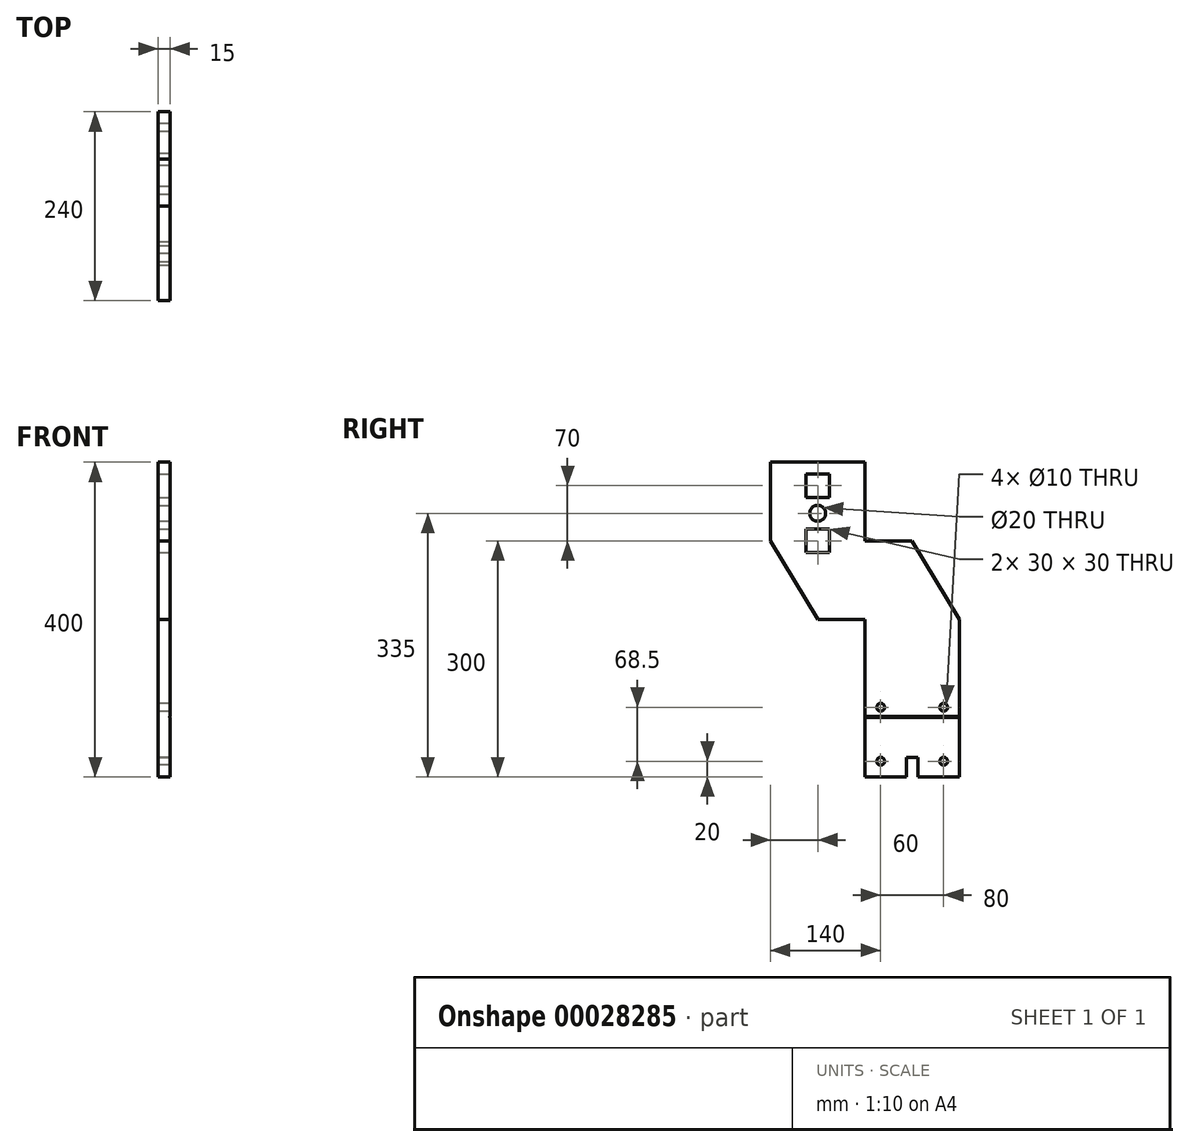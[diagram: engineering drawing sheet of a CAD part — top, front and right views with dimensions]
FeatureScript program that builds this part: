
annotation { "Feature Type Name" : "Feature", "Feature Type Description" : "" }
export const myFeature = defineFeature(function(context is Context, id is Id, definition is map)
    precondition{}
    {
        {
            var Q0;
            Q0=qCreatedBy(makeId("Right.planeOp"),FACE);
            var sketch = newSketch(context, id + "F0", { "sketchPlane" : qUnion([Q0])});
            skLineSegment(sketch, "E0.bottom", {"start": v(0, 0) * mm, "end": v(120, 0) * mm});
            skLineSegment(sketch, "E0.left", {"start": v(0, 0) * mm, "end": v(0, 200) * mm});
            skLineSegment(sketch, "E0.right", {"start": v(120, 0) * mm, "end": v(120, 200) * mm});
            skLineSegment(sketch, "E1", {"start": v(0, 200) * mm, "end": v(-60, 200) * mm});
            skLineSegment(sketch, "E2", {"start": v(0, 400) * mm, "end": v(-120, 400) * mm});
            skLineSegment(sketch, "E3", {"start": v(120, 200) * mm, "end": v(60, 300) * mm});
            skPoint(sketch, "E0.top.end.orphan", {"position": v(120, 400) * mm});
            skLineSegment(sketch, "E4", {"start": v(-60, 200) * mm, "end": v(-120, 300) * mm});
            skLineSegment(sketch, "E5", {"start": v(-120, 300) * mm, "end": v(-120, 400) * mm});
            skLineSegment(sketch, "E6", {"start": v(0, 400) * mm, "end": v(0, 300) * mm});
            skLineSegment(sketch, "E7", {"start": v(0, 300) * mm, "end": v(60, 300) * mm});
            skPoint(sketch, "E8.orphan", {"position": v(-180, 400) * mm});
            skSolve(sketch);
        }
        {
            var Q0;
            Q0=makeQuery(id+"F0.imprint","IMPRINT",FACE,{"disambiguationData":[TD([[makeQuery(id+"F0.imprint","IMPRINT",EDGE,{"derivedFrom":sQuery(id+"F0.wireOp",EDGE,"E0.bottom")}),1.0]])]});
            var sketch = newSketch(context, id + "F1", { "sketchPlane" : qUnion([Q0])});
            skCircle(sketch, "E9", {"center": v(20, 20) * mm, "radius": 5 * mm});
            skCircle(sketch, "E10.MirrorC", {"center": v(100, 20) * mm, "radius": 5 * mm});
            skCircle(sketch, "E11.MirrorC", {"center": v(100, 88.5) * mm, "radius": 5 * mm});
            skCircle(sketch, "E12.MirrorC", {"center": v(20, 88.5) * mm, "radius": 5 * mm});
            skSolve(sketch);
        }
        {
            var Q0;
            Q0=makeQuery(id+"F1.imprint","IMPRINT",FACE,{"disambiguationData":[TD([[makeQuery(id+"F1.imprint","IMPRINT",EDGE,{"derivedFrom":sQuery(id+"F1.wireOp",EDGE,"E9")}),-1.0]])]});
            extrude(context, id + "F2", {"entities" : qUnion([Q0]), "depth" : 15 * mm});
        }
        {
            var Q0;
            Q0=makeQuery(id+"F2.opExtrude","CAP_FACE",FACE,{"disambiguationData":[OSD([sQuery(id+"F0.wireOp",EDGE,"E0.bottom"),sQuery(id+"F0.wireOp",EDGE,"E0.top"),sQuery(id+"F0.wireOp",EDGE,"E0.left"),sQuery(id+"F0.wireOp",EDGE,"E0.right"),sQuery(id+"F1.wireOp",EDGE,"E9"),sQuery(id+"F1.wireOp",EDGE,"E10.MirrorC"),sQuery(id+"F1.wireOp",EDGE,"E11.MirrorC"),sQuery(id+"F1.wireOp",EDGE,"E12.MirrorC")])],"isStart":false});
            var sketch = newSketch(context, id + "F3", { "sketchPlane" : qUnion([Q0])});
            skLineSegment(sketch, "E13", {"start": v(0, 31.54) * mm, "end": v(120, 31.54) * mm});
            skLineSegment(sketch, "E14", {"start": v(0, 76.75) * mm, "end": v(120, 76.75) * mm});
            skLineSegment(sketch, "E15.0", {"start": v(0, 75.75) * mm, "end": v(120, 75.75) * mm});
            skLineSegment(sketch, "E16.0", {"start": v(0, 30.54) * mm, "end": v(120, 30.54) * mm});
            skLineSegment(sketch, "E17", {"start": v(0, 31.54) * mm, "end": v(0, 30.54) * mm});
            skLineSegment(sketch, "E18", {"start": v(0, 75.75) * mm, "end": v(0, 76.75) * mm});
            skLineSegment(sketch, "E19", {"start": v(120, 76.75) * mm, "end": v(120, 75.75) * mm});
            skLineSegment(sketch, "E20", {"start": v(120, 31.54) * mm, "end": v(120, 30.54) * mm});
            skSolve(sketch);
        }
        {
            var Q0;
            Q0=makeQuery(id+"F3.imprint","IMPRINT",FACE,{"disambiguationData":[TD([[makeQuery(id+"F3.imprint","IMPRINT",EDGE,{"derivedFrom":sQuery(id+"F3.wireOp",EDGE,"E14")}),-1.0]])]});
            extrude(context, id + "F4", {"entities" : qUnion([Q0]), "operationType" : NewBodyOperationType.REMOVE, "oppositeDirection" : true, "depth" : 1 * mm});
        }
        {
            var Q0;
            {var subQ0=sQuery(id+"F0.wireOp",EDGE,"E0.top");var subQ1=sQuery(id+"F0.wireOp",EDGE,"E0.left");var subQ2=sQuery(id+"F0.wireOp",EDGE,"E0.right");var subQ3=sQuery(id+"F1.wireOp",EDGE,"E11.MirrorC");var subQ4=sQuery(id+"F1.wireOp",EDGE,"E12.MirrorC");Q0=makeQuery(id+"F4.boolean.opBoolean","SPLIT",FACE,{"disambiguationData":[TD([makeQuery(id+"F2.opExtrude","SWEPT_FACE",FACE,{"disambiguationData":[OSD([subQ3])]})])],"derivedFrom":makeQuery(id+"F2.opExtrude","CAP_FACE",FACE,{"disambiguationData":[OSD([sQuery(id+"F0.wireOp",EDGE,"E0.bottom"),subQ0,subQ1,subQ2,sQuery(id+"F1.wireOp",EDGE,"E9"),sQuery(id+"F1.wireOp",EDGE,"E10.MirrorC"),subQ3,subQ4])],"isStart":false})});}
            var sketch = newSketch(context, id + "F5", { "sketchPlane" : qUnion([Q0])});
            skLineSegment(sketch, "E21.bottom", {"start": v(-75, 385) * mm, "end": v(-45, 385) * mm});
            skLineSegment(sketch, "E21.top", {"start": v(-75, 355) * mm, "end": v(-45, 355) * mm});
            skLineSegment(sketch, "E21.left", {"start": v(-75, 385) * mm, "end": v(-75, 355) * mm});
            skLineSegment(sketch, "E21.right", {"start": v(-45, 385) * mm, "end": v(-45, 355) * mm});
            skLineSegment(sketch, "E22.MirrorCS", {"start": v(-45, 285) * mm, "end": v(-45, 315) * mm});
            skLineSegment(sketch, "E23", {"start": v(-45, 315) * mm, "end": v(-75, 315) * mm});
            skLineSegment(sketch, "E24", {"start": v(-75, 315) * mm, "end": v(-75, 285) * mm});
            skLineSegment(sketch, "E25", {"start": v(-75, 285) * mm, "end": v(-45, 285) * mm});
            skLineSegment(sketch, "E26", {"start": v(-60, 315) * mm, "end": v(-60, 335) * mm});
            skCircle(sketch, "E27", {"center": v(-60, 335) * mm, "radius": 10 * mm});
            skSolve(sketch);
        }
        {
            var Q0;
            Q0 = qSketchRegion(id + "F5", true);
            extrude(context, id + "F6", {"entities" : qUnion([Q0]), "operationType" : NewBodyOperationType.REMOVE, "oppositeDirection" : true, "depth" : 25 * mm});
        }
        {
            var Q0;
            {var subQ1=sQuery(id+"F3.wireOp",EDGE,"E14");Q0=makeQuery(id+"F3.imprint","IMPRINT",FACE,{"disambiguationData":[TD([[makeQuery(id+"F3.imprint","IMPRINT",EDGE,{"derivedFrom":subQ1}),1.0]])]});}
            var sketch = newSketch(context, id + "F7", { "sketchPlane" : qUnion([Q0])});
            skLineSegment(sketch, "E28", {"start": v(67.58, 25.08) * mm, "end": v(52.58, 25.08) * mm});
            skLineSegment(sketch, "E29.0", {"start": v(67.58, 25.08) * mm, "end": v(67.58, 0) * mm});
            skLineSegment(sketch, "E30.0", {"start": v(52.58, 25.08) * mm, "end": v(52.58, 0) * mm});
            skLineSegment(sketch, "E31", {"start": v(67.58, 0) * mm, "end": v(52.58, 0) * mm});
            skSolve(sketch);
        }
        {
            var Q0;
            Q0 = qSketchRegion(id + "F7", true);
            extrude(context, id + "F8", {"entities" : qUnion([Q0]), "operationType" : NewBodyOperationType.REMOVE, "oppositeDirection" : true, "depth" : 25 * mm});
        }
    });
